# Revit family: Sanitary_Showers_AXOR_18356USA-AXOR-ShowerSolutions-Thermostatic-module-Select-53090-for-concealed-installation-for-3-functions
name_source: partatom
category: Plumbing Fixtures
revit_build: Autodesk Revit 2018 (Build: 20190510_1515(x64)
units: mm (PartAtom-declared; Revit-internal decimal feet)

## family parameters
Always vertical = No
Cut with Voids When Loaded = No
OmniClass Number = 23.31.17.00
OmniClass Title = Showers
Part Type = Normal
Room Calculation Point = No
Round Connector Dimension = Use Diameter
Shared = No
Work Plane-Based = Yes

## types (1)
- 821 Brushed Nickel
    Always visible = Yes
    BIMobject category = Showers
    Default Elevation = 1219.2 mm  [stored 4 ft]
    Description = AXOR ShowerSolutions Thermostatic module Select 530/90 for concealed installation for 3 functions
    Edition number = 1
    IFC Classification = Sanitary Terminal
    Main Material = Axor - Metal - 821 Brushed Nickel
    Manufacturer = Axor
    Manufacturer name = AXOR
    Model = 18356USA AXOR ShowerSolutions Thermostatic module Select 530/90 for concealed installation for 3 functions
    OmniClass Code = 23-31 17 00
    OmniClass Description = Showers
    Product Guid = 442a2a14-48eb-4b84-956f-c2741b815423
    Product SKU = 18356USA
    Product data url = https://bimobject.com
    Product family = AXOR ShowerSolutions
    Product group = Shower thermostat
    Product name = 18356USA AXOR ShowerSolutions Thermostatic module Select 530/90 for concealed installation for 3 functions
    Product url = https://www.axor-design.com
    QR code = https://bimobject.com
    URL = https://www.axor-design.com
    Weight Net (Kg) = 4,4

note: [stored X ft] marks values corroborated as IEEE doubles in the binary element streams (Revit-internal decimal feet)

## geometry (parser evidence)
native form markers: Sweep x4
no freeform markers — native parametric forms only
